# Revit family: LAMP_OCULT SYSTEM SPOTLIGHT 500 (DALI)
name_source: partatom
category: Luminarias
revit_build: Autodesk Revit 2015 (Build: 20140606_1530(x64)
units: mm (PartAtom-declared; Revit-internal decimal feet)

## types (12) — shared parameters
CRI = 80
Comentarios de tipo = Availability of tilting between 0º and 90º, rotation between 0º and 355º and change ring color when placed in a project.
Diameter = 40 mm  [stored 0.131234 ft]
Elevación por defecto = 1219 mm
Fabricante = LAMP
Gear = Adjustable DALI
Height = 78 mm  [stored 0.255906 ft]
IEE = A+
Installation instructions = https://www.lamp.es
Insulation class = I
LED Lifetime = 50.000 L90
Lamp = HIGH POWER LED
Last update = 31/07/2019
Luminaire type = Indoor - Spotlight
MacAdam = 3
Manufacturer URL = http://www.lamp.es
Manufacturer country = Spain
Manufacturer name = LAMP
Material suspension = Panel de metal
Model explanation = Availability of tilting between 0º and 90º, rotation between 0º and 355º and change ring color when placed in a project.
Plum = 6 W
Power = 4 W
Power Supply = 100-240V 50/60Hz
Product URL = https://www.lamp.es
Product datasheet = http://www.lamp.es
Protection rating = IP20
Type = HIGH POWER CREE
Weight = 0.33 kg

## per-type parameters (varying)
| type | Descripción | Efficacy | Finish | Initial color | Initial intensity | Material perfil | Modelo | Photometric web file | Product code |
| 314LM 3000 SPOT BLACK | OCULT SYS. SPOT 500 WW SP DALI BK/BK. | 52 lm/W | Texturised black RAL 9011 | 3000 K | 314 lm | LAMP_Aluminio Ocult Pendular NG | OS1SP05SP830DBB | Modelo spotlight : 314LM 3000 SPOT BLACK | OS1SP05SP830DBB |
| 314LM 3000 SPOT WHITE | OCULT SYS. SPOT 500 WW SP DALI BK/WH. | 52 lm/W | Texturised matt white | 3000 K | 314 lm | LAMP_Aluminio Ocult Pendular BL | OS1SP05SP830DBW | Modelo spotlight : 314LM 3000 SPOT WHITE | OS1SP05SP830DBW |
| 324LM 3000 FLOOD BLACK | OCULT SYS. SPOT 500 WW FL DALI BK/BK. | 54 lm/W | Texturised black RAL 9011 | 3000 K | 324 lm | LAMP_Aluminio Ocult Pendular NG | OS1SP05FL830DBB | Modelo spotlight : 324LM 3000 FLOOD BLACK | OS1SP05FL830DBB |
| 324LM 3000 FLOOD WHITE | OCULT SYS. SPOT 500 WW FL DALI BK/WH. | 54 lm/W | Texturised matt white | 3000 K | 324 lm | LAMP_Aluminio Ocult Pendular BL | OS1SP05FL830DBW | Modelo spotlight : 324LM 3000 FLOOD WHITE | OS1SP05FL830DBW |
| 330LM 3000 MEDIUM FLOOD BLACK | OCULT SYS. SPOT 500 WW MFL DALI BK/BK. | 55 lm/W | Texturised black RAL 9011 | 3000 K | 330 lm | LAMP_Aluminio Ocult Pendular NG | OS1SP05MF830DBB | Modelo spotlight : 330LM 3000 MEDIUM FLOOD BLACK | OS1SP05MF830DBB |
| 330LM 3000 MEDIUM FLOOD WHITE | OCULT SYS. SPOT 500 WW MFL DALI BK/WH. | 55 lm/W | Texturised matt white | 3000 K | 330 lm | LAMP_Aluminio Ocult Pendular BL | OS1SP05MF830DBW | Modelo spotlight : 330LM 3000 MEDIUM FLOOD WHITE | OS1SP05MF830DBW |
| 339LM 4000 SPOT BLACK | OCULT SYS. SPOT 500 NW SP DALI BK/BK. | 57 lm/W | Texturised black RAL 9011 | 4000 K | 339 lm | LAMP_Aluminio Ocult Pendular NG | OS1SP05SP840DBB | Modelo spotlight : 339LM 4000 SPOT BLACK | OS1SP05SP840DBB |
| 339LM 4000 SPOT WHITE | OCULT SYS. SPOT 500 NW SP DALI BK/WH. | 57 lm/W | Texturised matt white | 4000 K | 339 lm | LAMP_Aluminio Ocult Pendular BL | OS1SP05SP840DBW | Modelo spotlight : 339LM 4000 SPOT WHITE | OS1SP05SP840DBW |
| 349LM 4000 FLOOD BLACK | OCULT SYS. SPOT 500 NW FL DALI BK/BK. | 58 lm/W | Texturised black RAL 9011 | 4000 K | 349 lm | LAMP_Aluminio Ocult Pendular NG | OS1SP05FL840DBB | Modelo spotlight : 349LM 4000 FLOOD BLACK | OS1SP05FL840DBB |
| 349LM 4000 FLOOD WHITE | OCULT SYS. SPOT 500 NW FL DALI BK/WH. | 58 lm/W | Texturised matt white | 4000 K | 349 lm | LAMP_Aluminio Ocult Pendular BL | OS1SP05FL840DBW | Modelo spotlight : 349LM 4000 FLOOD WHITE | OS1SP05FL840DBW |
| 356LM 4000 MEDIUM FLOOD BLACK | OCULT SYS. SPOT 500 NW MFL DALI BK/BK. | 59 lm/W | Texturised black RAL 9011 | 4000 K | 356 lm | LAMP_Aluminio Ocult Pendular NG | OS1SP05MF840DBB | Modelo spotlight : 356LM 4000 MEDIUM FLOOD BLACK | OS1SP05MF840DBB |
| 356LM 4000 MEDIUM FLOOD WHITE | OCULT SYS. SPOT 500 NW MFL DALI BK/WH. | 59 lm/W | Texturised matt white | 4000 K | 356 lm | LAMP_Aluminio Ocult Pendular BL | OS1SP05MF840DBW | Modelo spotlight : 356LM 4000 MEDIUM FLOOD WHITE | OS1SP05MF840DBW |

note: [stored X ft] marks values corroborated as IEEE doubles in the binary element streams (Revit-internal decimal feet)
